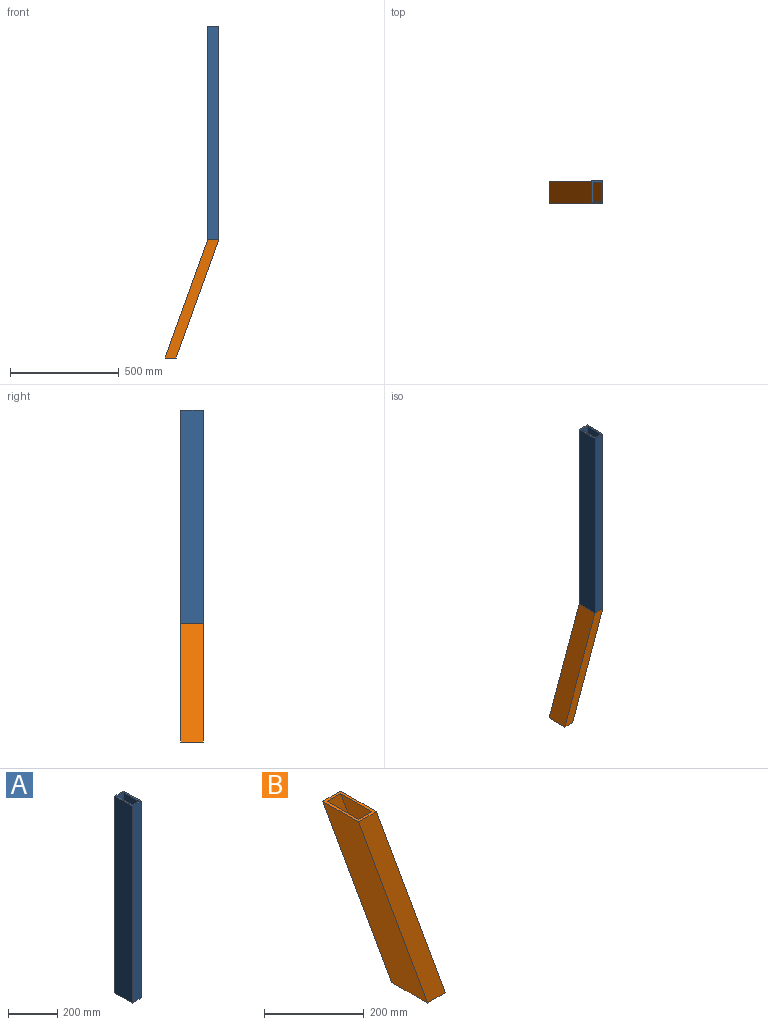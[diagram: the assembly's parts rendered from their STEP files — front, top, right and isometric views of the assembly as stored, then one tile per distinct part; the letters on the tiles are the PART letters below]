
ASSEMBLY  parts=2 mates=1
PART A: 10 faces, bbox 50.8x101.6x980.4 mm
  f0: plane 980.44x88.9mm, normal (1,0,0), area 87161.1mm2, adj f1,f3,f4,f5
  f1: plane 980.44x38.1mm, normal (0,-1,0), area 37354.8mm2, adj f0,f2,f4,f5
  f2: plane 980.44x88.9mm, normal (-1,0,0), area 87161.1mm2, adj f1,f3,f4,f5
  f3: plane 980.44x38.1mm, normal (0,1,0), area 37354.8mm2, adj f0,f2,f4,f5
  f4: plane 101.6x50.8mm, normal (0,0,-1), area 1774.2mm2, adj f0,f1,f2,f3,f6,f7,f8,f9
  f5: plane 101.6x50.8mm, normal (0,0,1), area 1774.2mm2, adj f0,f1,f2,f3,f6,f7,f8,f9
  f6: plane 980.44x50.8mm, normal (0,1,0), area 49806.4mm2, adj f4,f5,f7,f9
  f7: plane 980.44x101.6mm, normal (-1,0,0), area 99612.7mm2, adj f4,f5,f6,f8
  f8: plane 980.44x50.8mm, normal (0,-1,0), area 49806.4mm2, adj f4,f5,f7,f9
  f9: plane 980.44x101.6mm, normal (1,0,0), area 99612.7mm2, adj f4,f5,f6,f8
PART B: 10 faces, bbox 246.9x101.6x543.6 mm
  f0: plane 543.56x196.09mm, normal (0.94,0,0.34), area 51370.9mm2, adj f1,f3,f4,f5
  f1: plane 543.56x234.19mm, normal (0,-1,0), area 20709.6mm2, adj f0,f2,f4,f5
  f2: plane 543.56x196.09mm, normal (-0.94,0,-0.34), area 51370.9mm2, adj f1,f3,f4,f5
  f3: plane 543.56x234.19mm, normal (0,1,0), area 20709.6mm2, adj f0,f2,f4,f5
  f4: plane 101.6x50.8mm, normal (0,0,-1), area 1774.2mm2, adj f0,f1,f2,f3,f6,f7,f8,f9
  f5: plane 101.6x50.8mm, normal (0,0,1), area 1774.2mm2, adj f0,f1,f2,f3,f6,f7,f8,f9
  f6: plane 543.56x246.89mm, normal (0,1,0), area 27612.8mm2, adj f4,f5,f7,f9
  f7: plane 543.56x196.09mm, normal (-0.94,0,-0.34), area 58709.6mm2, adj f4,f5,f6,f8
  f8: plane 543.56x246.89mm, normal (0,-1,0), area 27612.8mm2, adj f4,f5,f7,f9
  f9: plane 543.56x196.09mm, normal (0.94,0,0.34), area 58709.6mm2, adj f4,f5,f6,f8
PLACE A t=(2576.59,0,0)mm
PLACE B rot(axis=(0,0,1),180deg) t=(-2133.6,0,0)mm
MATE fastened A.f4 <-> B.f5  axis (0,0,-1) through (240.54,0,543.56)mm
